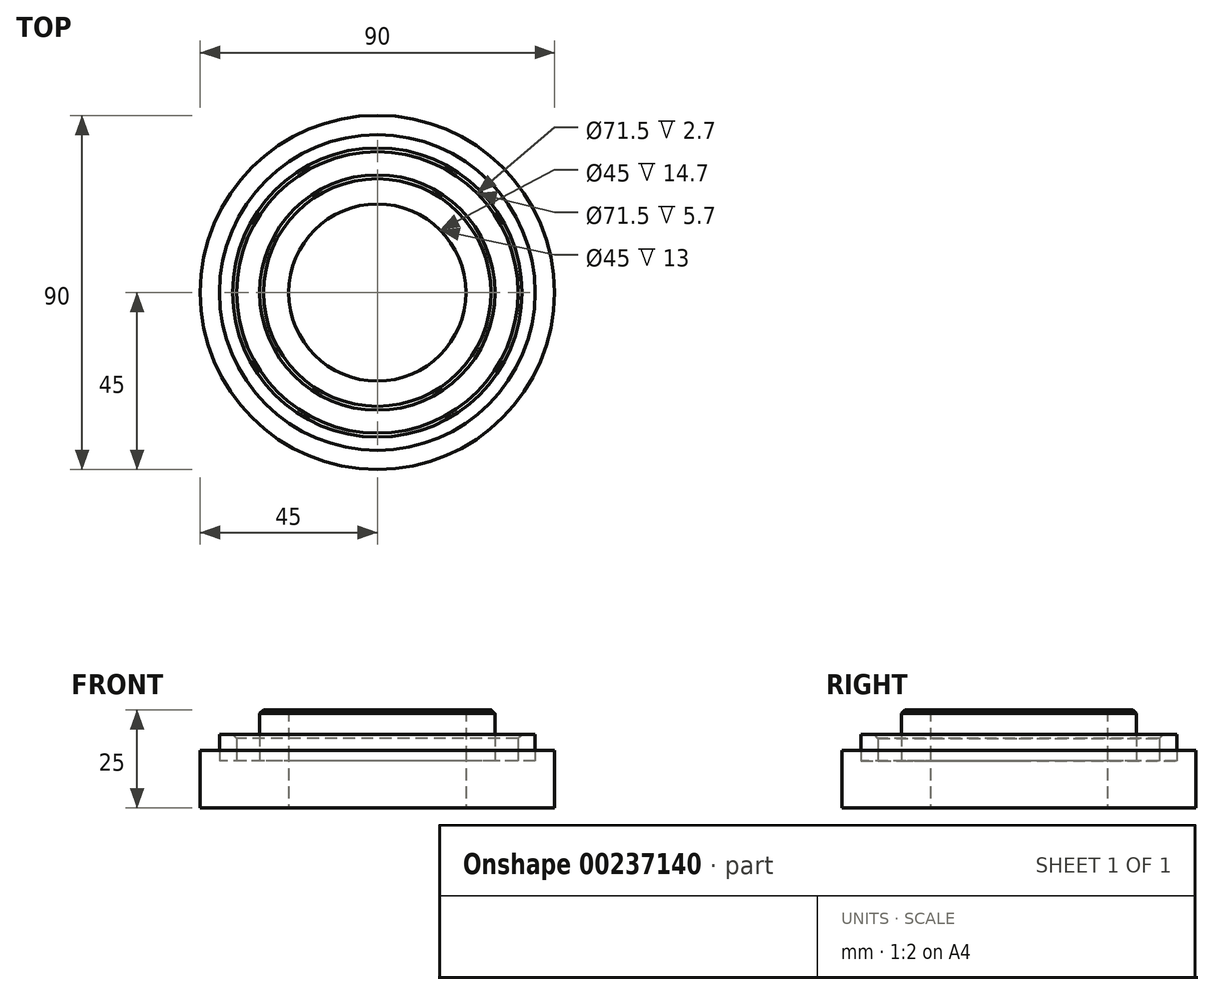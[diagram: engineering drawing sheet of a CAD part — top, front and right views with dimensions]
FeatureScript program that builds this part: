
annotation { "Feature Type Name" : "Feature", "Feature Type Description" : "" }
export const myFeature = defineFeature(function(context is Context, id is Id, definition is map)
    precondition{}
    {
        {
            var Q0;
            Q0=qCreatedBy(makeId("Top.planeOp"),FACE);
            var sketch = newSketch(context, id + "F0", { "sketchPlane" : qUnion([Q0])});
            skCircle(sketch, "E0", {"center": v(0, 0) * mm, "radius": 40.1 * mm});
            skCircle(sketch, "E1", {"center": v(0, 0) * mm, "radius": 29.9 * mm});
            skCircle(sketch, "E2", {"center": v(0, 0) * mm, "radius": 35.75 * mm});
            skSolve(sketch);
        }
        {
            var Q0;
            Q0=qCreatedBy(makeId("Top.planeOp"),FACE);
            var sketch = newSketch(context, id + "F1", { "sketchPlane" : qUnion([Q0])});
            skCircle(sketch, "E3", {"center": v(0, 0) * mm, "radius": 45 * mm});
            skSolve(sketch);
        }
        {
            var Q0;
            Q0=qCreatedBy(makeId("Top.planeOp"),FACE);
            var sketch = newSketch(context, id + "F2", { "sketchPlane" : qUnion([Q0])});
            skCircle(sketch, "E4", {"center": v(0, 0) * mm, "radius": 22.5 * mm});
            skSolve(sketch);
        }
        {
            var Q0;
            Q0=makeQuery(id+"F0.imprint","IMPRINT",FACE,{"disambiguationData":[TD([[makeQuery(id+"F0.imprint","IMPRINT",EDGE,{"derivedFrom":sQuery(id+"F0.wireOp",EDGE,"E1")}),1.0]])]});
            var Q1;
            Q1=makeQuery(id+"F0.imprint","IMPRINT",FACE,{"disambiguationData":[TD([[makeQuery(id+"F0.imprint","IMPRINT",EDGE,{"derivedFrom":sQuery(id+"F0.wireOp",EDGE,"E0")}),1.0]])]});
            extrude(context, id + "F3", {"entities" : qUnion([Q0, Q1]), "depth" : 6.7 * mm});
        }
        {
            var Q0;
            Q0 = qSketchRegion(id + "F1", true);
            extrude(context, id + "F4", {"entities" : qUnion([Q0]), "oppositeDirection" : true, "depth" : 12 * mm, "hasSecondDirection" : true, "secondDirectionOppositeDirection" : false, "secondDirectionDepth" : 2.7 * mm});
        }
        {
            var Q0;
            Q0=makeQuery(id+"F0.imprint","IMPRINT",FACE,{"disambiguationData":[TD([[makeQuery(id+"F0.imprint","IMPRINT",EDGE,{"derivedFrom":sQuery(id+"F0.wireOp",EDGE,"E1")}),-1.0]])]});
            var Q1;
            Q1=sQuery(id+"F0.wireOp",EDGE,"E0");
            var Q2;
            Q2=sQuery(id+"F0.wireOp",EDGE,"E2");
            extrude(context, id + "F5", {"entities" : qUnion([Q0]), "operationType" : NewBodyOperationType.REMOVE, "surfaceEntities" : qUnion([Q1, Q2]), "depth" : 6.7 * mm});
        }
        {
            var Q0;
            Q0=makeQuery(id+"F3.opExtrude","CAP_EDGE",EDGE,{"disambiguationData":[OSD([sQuery(id+"F0.wireOp",EDGE,"E2")])],"isStart":false});
            chamfer(context, id + "F6", {"entities" : qUnion([Q0]), "width" : 1 * mm, "tangentPropagation" : true});
        }
        {
            var Q0;
            Q0=makeQuery(id+"F3.opExtrude","CAP_FACE",FACE,{"disambiguationData":[OSD([sQuery(id+"F0.wireOp",EDGE,"E1")])],"isStart":false});
            extrude(context, id + "F7", {"entities" : qUnion([Q0]), "operationType" : NewBodyOperationType.ADD, "depth" : 6.3 * mm});
        }
        {
            var Q0;
            Q0=makeQuery(id+"F7.opExtrude","CAP_FACE",FACE,{"disambiguationData":[OSD([sQuery(id+"F0.wireOp",EDGE,"E1")])],"isStart":false});
            chamfer(context, id + "F8", {"entities" : qUnion([Q0]), "width" : 1 * mm, "tangentPropagation" : true});
        }
        {
            var Q0;
            Q0=makeQuery(id+"F2.imprint","IMPRINT",FACE,{"disambiguationData":[TD([[makeQuery(id+"F2.imprint","IMPRINT",EDGE,{"derivedFrom":sQuery(id+"F2.wireOp",EDGE,"E4")}),1.0]])]});
            var Q1;
            Q1=sQuery(id+"F2.wireOp",EDGE,"E4");
            extrude(context, id + "F9", {"entities" : qUnion([Q0]), "operationType" : NewBodyOperationType.REMOVE, "surfaceEntities" : qUnion([Q1]), "depth" : 13 * mm, "hasSecondDirection" : true, "secondDirectionOppositeDirection" : true, "secondDirectionDepth" : 12 * mm});
        }
    });
